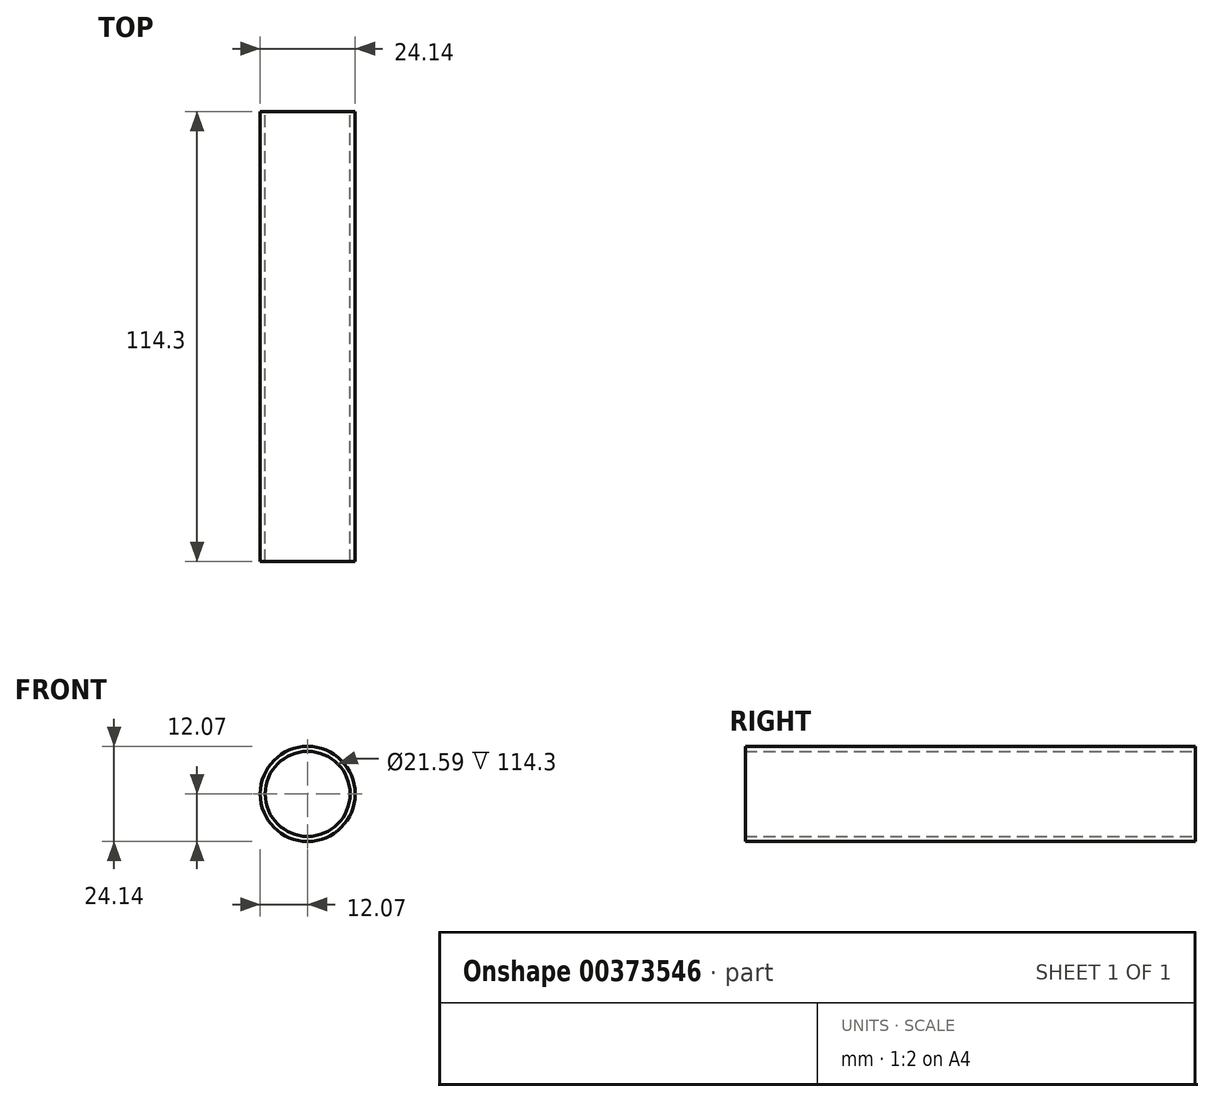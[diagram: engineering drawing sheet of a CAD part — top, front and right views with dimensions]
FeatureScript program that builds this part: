
annotation { "Feature Type Name" : "Feature", "Feature Type Description" : "" }
export const myFeature = defineFeature(function(context is Context, id is Id, definition is map)
    precondition{}
    {
        {
            var Q0;
            Q0=qCreatedBy(makeId("Front.planeOp"),FACE);
            var sketch = newSketch(context, id + "F0", { "sketchPlane" : qUnion([Q0])});
            skCircle(sketch, "E0", {"center": v(0, 0) * mm, "radius": 12.07 * mm});
            skCircle(sketch, "E1", {"center": v(0, 0) * mm, "radius": 10.8 * mm});
            skSolve(sketch);
        }
        {
            var Q0;
            Q0=makeQuery(id+"F0.imprint","IMPRINT",FACE,{"disambiguationData":[TD([[makeQuery(id+"F0.imprint","IMPRINT",EDGE,{"derivedFrom":sQuery(id+"F0.wireOp",EDGE,"E0")}),1.0]])]});
            extrude(context, id + "F1", {"entities" : qUnion([Q0]), "depth" : 114.3 * mm});
        }
    });
